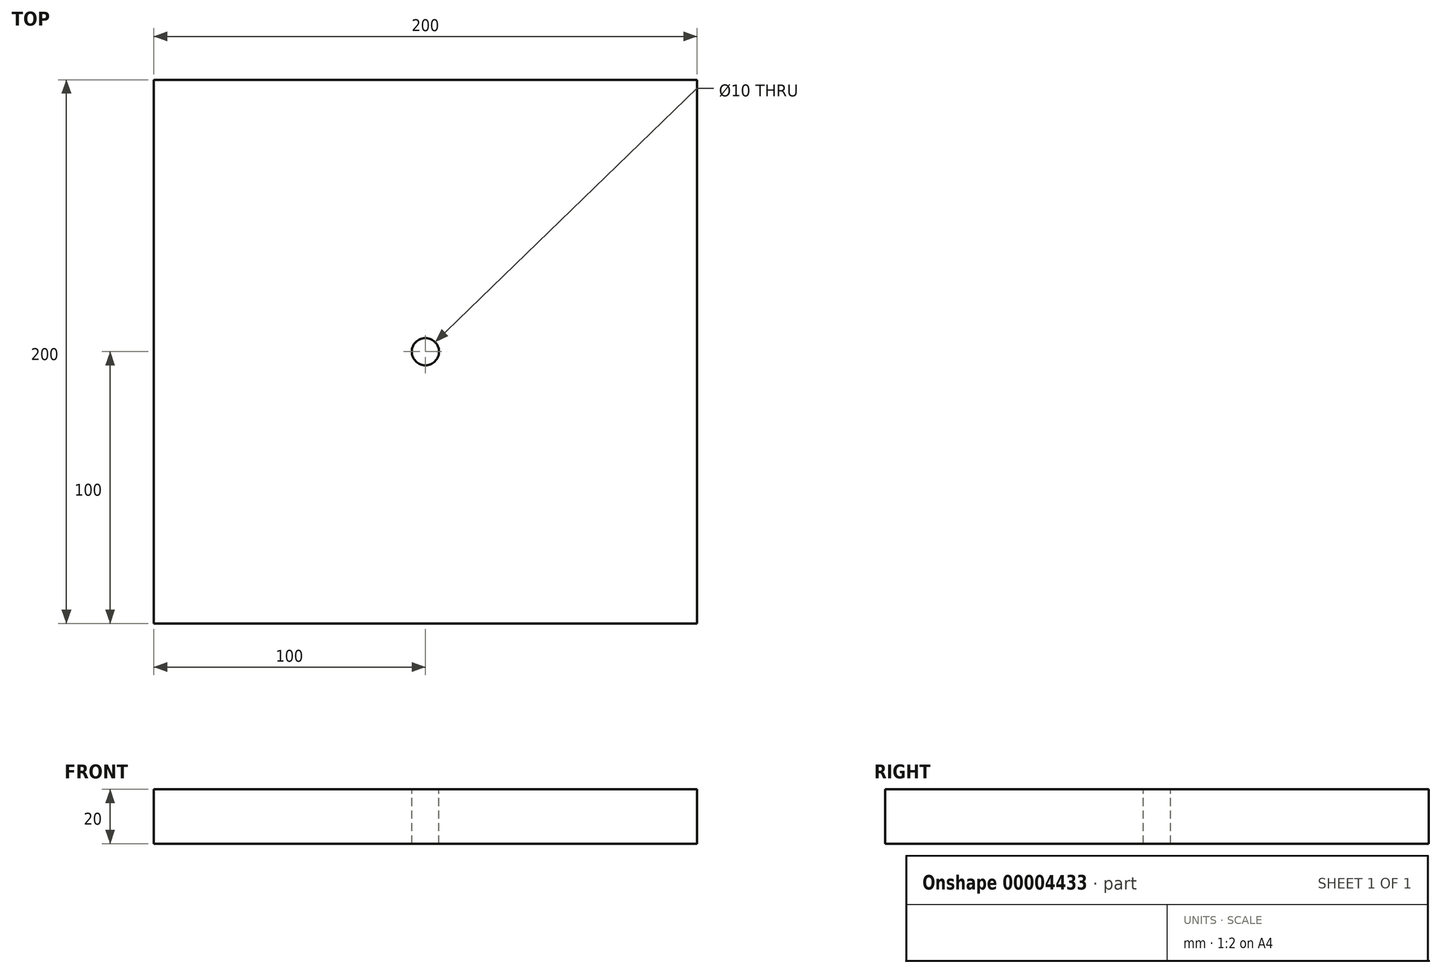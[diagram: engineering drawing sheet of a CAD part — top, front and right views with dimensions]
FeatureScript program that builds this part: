
annotation { "Feature Type Name" : "Feature", "Feature Type Description" : "" }
export const myFeature = defineFeature(function(context is Context, id is Id, definition is map)
    precondition{}
    {
        {
            var Q0;
            Q0=qCreatedBy(makeId("Top.planeOp"),FACE);
            var sketch = newSketch(context, id + "F0", { "sketchPlane" : qUnion([Q0])});
            skLineSegment(sketch, "E0.bottom", {"start": v(0, 0) * mm, "end": v(200, 0) * mm});
            skLineSegment(sketch, "E0.top", {"start": v(0, 200) * mm, "end": v(200, 200) * mm});
            skLineSegment(sketch, "E0.left", {"start": v(0, 0) * mm, "end": v(0, 200) * mm});
            skLineSegment(sketch, "E0.right", {"start": v(200, 0) * mm, "end": v(200, 200) * mm});
            skSolve(sketch);
        }
        {
            var Q0;
            Q0=makeQuery(id+"F0.imprint","IMPRINT",FACE,{"disambiguationData":[TD([[makeQuery(id+"F0.imprint","IMPRINT",EDGE,{"derivedFrom":sQuery(id+"F0.wireOp",EDGE,"E0.bottom")}),1.0]])]});
            extrude(context, id + "F1", {"entities" : qUnion([Q0]), "depth" : 20 * mm});
        }
        {
            var Q0;
            Q0=makeQuery(id+"F1.opExtrude","CAP_FACE",FACE,{"disambiguationData":[OSD([sQuery(id+"F0.wireOp",EDGE,"E0.bottom"),sQuery(id+"F0.wireOp",EDGE,"E0.top"),sQuery(id+"F0.wireOp",EDGE,"E0.left"),sQuery(id+"F0.wireOp",EDGE,"E0.right")])],"isStart":false});
            var sketch = newSketch(context, id + "F2", { "sketchPlane" : qUnion([Q0])});
            skCircle(sketch, "E1", {"center": v(100, 100) * mm, "radius": 5 * mm});
            skSolve(sketch);
        }
        {
            var Q0;
            Q0=makeQuery(id+"F2.imprint","IMPRINT",FACE,{"disambiguationData":[TD([[makeQuery(id+"F2.imprint","IMPRINT",EDGE,{"derivedFrom":sQuery(id+"F2.wireOp",EDGE,"E1")}),1.0]])]});
            extrude(context, id + "F3", {"entities" : qUnion([Q0]), "operationType" : NewBodyOperationType.REMOVE, "endBound" : BoundingType.THROUGH_ALL, "oppositeDirection" : true, "depth" : 25 * mm});
        }
    });
